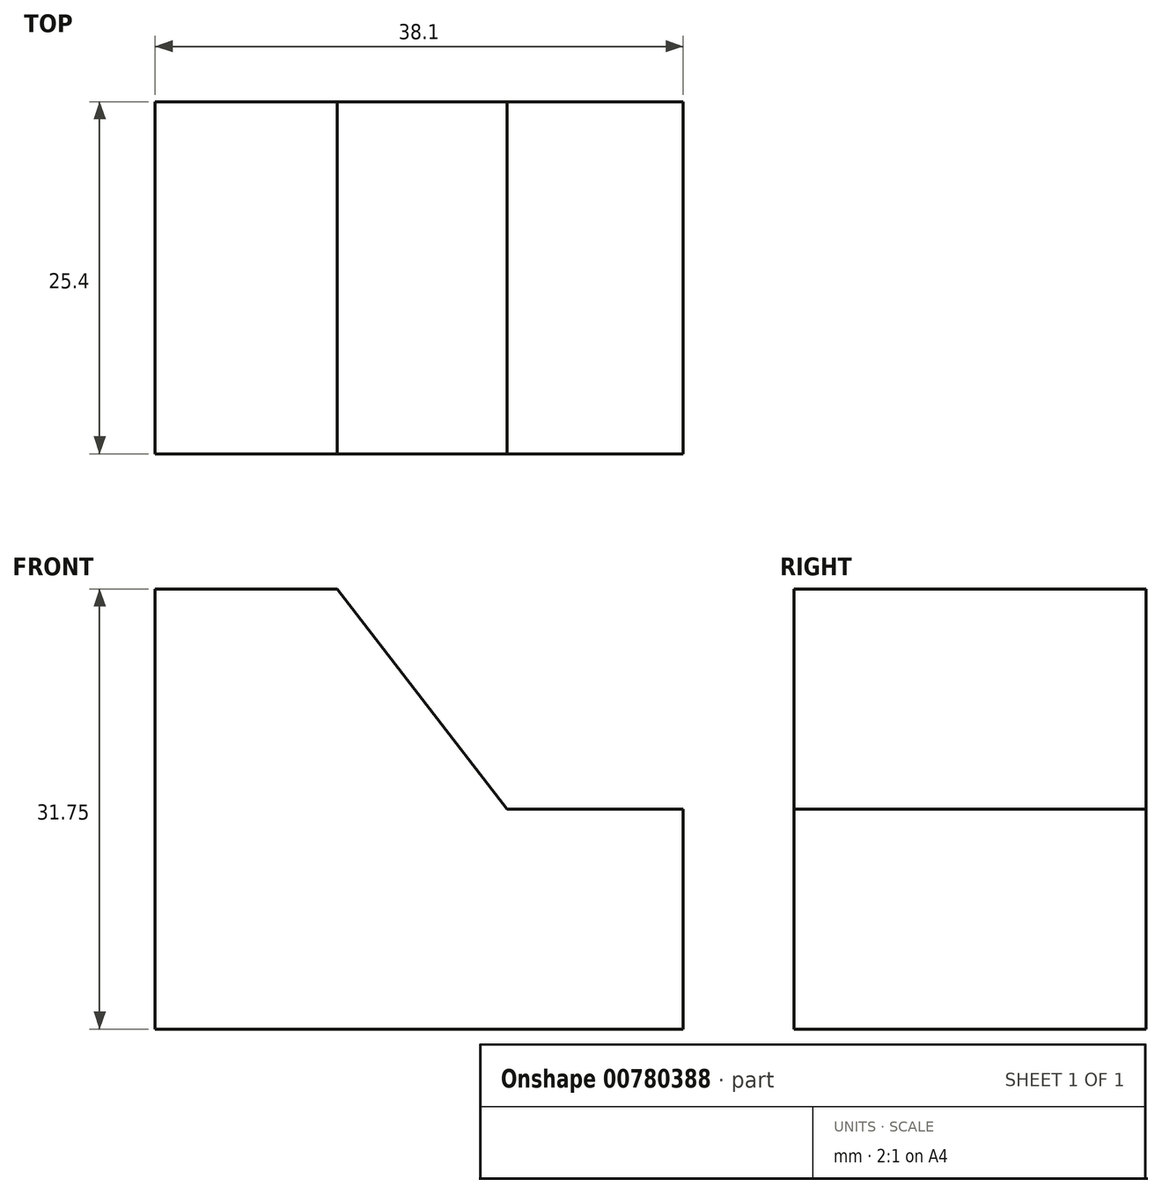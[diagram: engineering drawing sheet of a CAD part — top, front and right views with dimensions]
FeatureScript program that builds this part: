
annotation { "Feature Type Name" : "Feature", "Feature Type Description" : "" }
export const myFeature = defineFeature(function(context is Context, id is Id, definition is map)
    precondition{}
    {
        {
            var Q0;
            Q0=qCreatedBy(makeId("Front.planeOp"),FACE);
            var sketch = newSketch(context, id + "F0", { "sketchPlane" : qUnion([Q0])});
            skLineSegment(sketch, "E0", {"start": v(0, 0) * mm, "end": v(-38.1, 0) * mm});
            skLineSegment(sketch, "E1", {"start": v(-38.1, 0) * mm, "end": v(-38.1, 31.75) * mm});
            skLineSegment(sketch, "E2", {"start": v(-38.1, 31.75) * mm, "end": v(-24.96, 31.75) * mm});
            skLineSegment(sketch, "E3", {"start": v(0, 0) * mm, "end": v(0, 15.88) * mm});
            skPoint(sketch, "E3.endSnap0", {"position": v(-38.1, 15.88) * mm});
            skLineSegment(sketch, "E4", {"start": v(0, 15.88) * mm, "end": v(-12.7, 15.88) * mm});
            skLineSegment(sketch, "E5", {"start": v(-12.7, 15.88) * mm, "end": v(-24.96, 31.75) * mm});
            skSolve(sketch);
        }
        {
            var Q0;
            Q0=makeQuery(id+"F0.imprint","IMPRINT",FACE,{"disambiguationData":[TD([[makeQuery(id+"F0.imprint","IMPRINT",EDGE,{"derivedFrom":sQuery(id+"F0.wireOp",EDGE,"E0")}),-1.0]])]});
            extrude(context, id + "F1", {"entities" : qUnion([Q0]), "depth" : 25.4 * mm, "offsetDistance" : 25.4 * mm});
        }
    });
